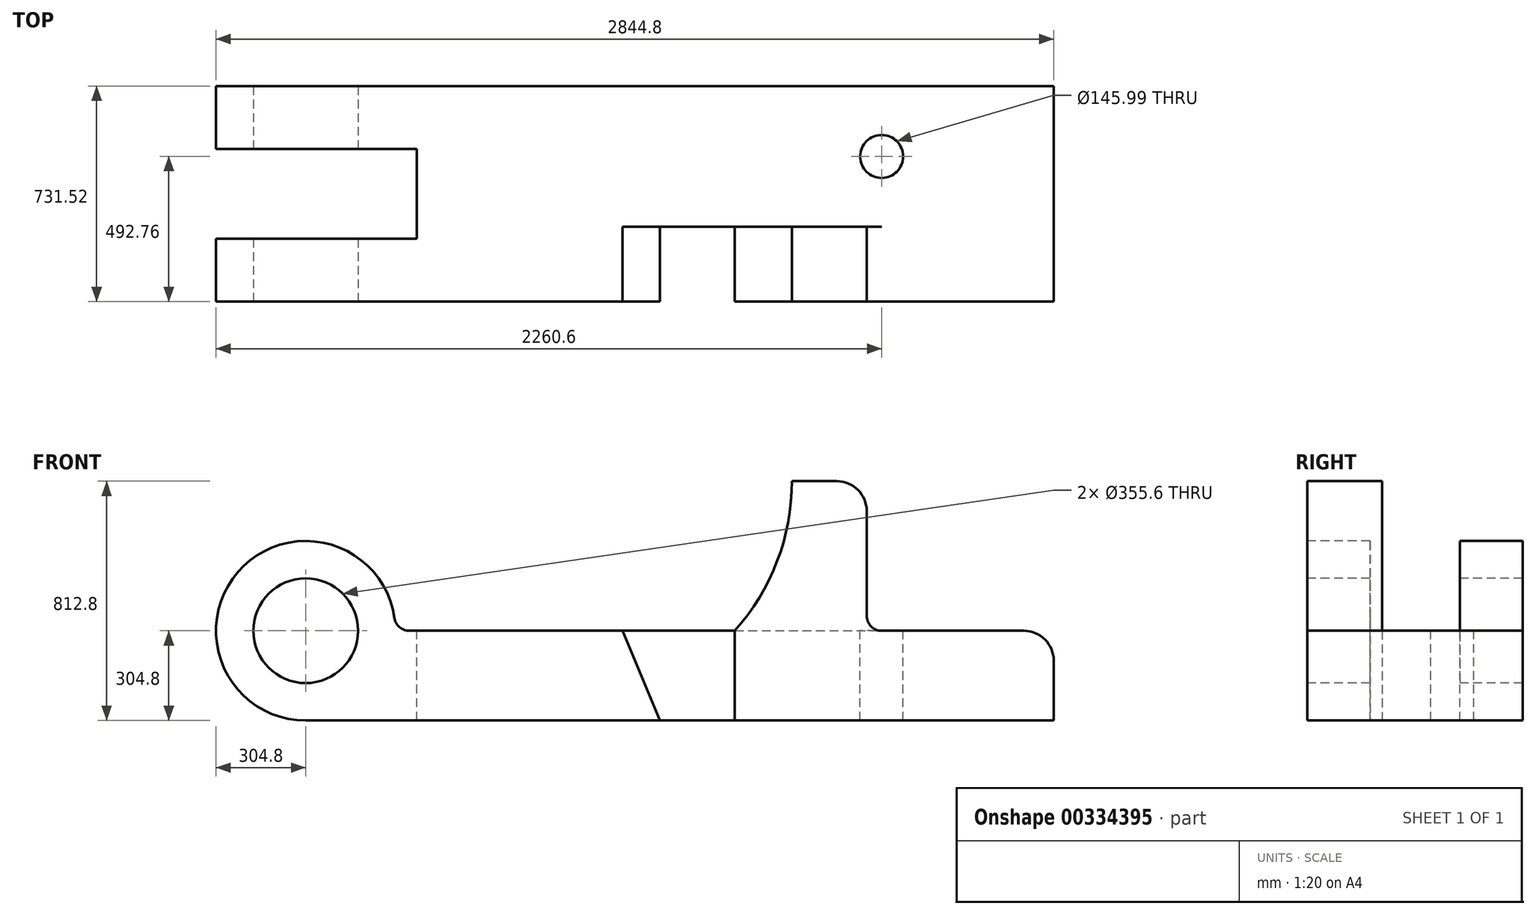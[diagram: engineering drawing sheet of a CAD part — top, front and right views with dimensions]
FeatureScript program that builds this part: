
annotation { "Feature Type Name" : "Feature", "Feature Type Description" : "" }
export const myFeature = defineFeature(function(context is Context, id is Id, definition is map)
    precondition{}
    {
        {
            var Q0;
            Q0=qCreatedBy(makeId("Front.planeOp"),FACE);
            var sketch = newSketch(context, id + "F0", { "sketchPlane" : qUnion([Q0])});
            skCircle(sketch, "E0", {"center": v(0, 0) * mm, "radius": 177.8 * mm});
            skLineSegment(sketch, "E1.top", {"start": v(0, -304.8) * mm, "end": v(1456.94, -304.8) * mm});
            skLineSegment(sketch, "E1.left", {"start": v(0, 0) * mm, "end": v(0, -304.8) * mm});
            skLineSegment(sketch, "E2", {"start": v(1651, 508) * mm, "end": v(1803.4, 508) * mm});
            skLineSegment(sketch, "E3", {"start": v(1905, 406.4) * mm, "end": v(1905, 50.8) * mm});
            skLineSegment(sketch, "E4", {"start": v(1955.8, 0) * mm, "end": v(2438.4, 0) * mm});
            skLineSegment(sketch, "E5", {"start": v(2540, -101.6) * mm, "end": v(2540, -304.8) * mm});
            skLineSegment(sketch, "E6", {"start": v(2540, -304.8) * mm, "end": v(1456.94, -304.8) * mm});
            skLineSegment(sketch, "E7", {"start": v(0, 0) * mm, "end": v(0, 1250.25) * mm});
            skLineSegment(sketch, "E8", {"start": v(351.95, 0) * mm, "end": v(1456.94, 0) * mm});
            skLineSegment(sketch, "E9", {"start": v(1075.94, 0) * mm, "end": v(1202.94, -304.8) * mm});
            skArc(sketch, "E10", {"start": v(1456.94, 0) * mm, "mid": v(1600.83, 236.1) * mm, "end": v(1651, 508) * mm});
            skLineSegment(sketch, "E11", {"start": v(1456.94, 0) * mm, "end": v(1456.94, -304.8) * mm});
            skLineSegment(sketch, "E12", {"start": v(1456.94, -304.8) * mm, "end": v(1456.94, -304.8) * mm});
            skArc(sketch, "E13", {"start": v(301.67, 43.54) * mm, "mid": v(-230.4, 199.54) * mm, "end": v(0, -304.8) * mm});
            skPoint(sketch, "E14.visualSharp", {"position": v(1905, 508) * mm});
            skArc(sketch, "E14.filletArc", {"start": v(1905, 406.4) * mm, "mid": v(1875.24, 478.24) * mm, "end": v(1803.4, 508) * mm});
            skPoint(sketch, "E15.visualSharp", {"position": v(1905, 0) * mm});
            skArc(sketch, "E15.filletArc", {"start": v(1905, 50.8) * mm, "mid": v(1919.88, 14.88) * mm, "end": v(1955.8, 0) * mm});
            skPoint(sketch, "E16.visualSharp", {"position": v(2540, 0) * mm});
            skArc(sketch, "E16.filletArc", {"start": v(2540, -101.6) * mm, "mid": v(2510.24, -29.76) * mm, "end": v(2438.4, 0) * mm});
            skLineSegment(sketch, "E17", {"start": v(1456.94, 0) * mm, "end": v(1955.8, 0) * mm});
            skPoint(sketch, "E18.visualSharp", {"position": v(304.8, 0) * mm});
            skArc(sketch, "E18.filletArc", {"start": v(301.67, 43.54) * mm, "mid": v(318.7, 12.4) * mm, "end": v(351.95, 0) * mm});
            skSolve(sketch);
        }
        {
            var Q0;
            {var subQ0=sQuery(id+"F0.wireOp",EDGE,"E1.left");var subQ1=sQuery(id+"F0.wireOp",EDGE,"E0");var subQ2=makeQuery(id+"F0.imprint","INTERSECT",VERTEX,{"derivedFrom":[subQ1,subQ0]});Q0=makeQuery(id+"F0.imprint","IMPRINT",FACE,{"disambiguationData":[TD([[makeQuery(id+"F0.imprint","IMPRINT",EDGE,{"disambiguationData":[TD([[subQ2,1.0]])],"derivedFrom":subQ1}),-1.0]])]});}
            var Q1;
            {var subQ2=sQuery(id+"F0.wireOp",EDGE,"E9");Q1=makeQuery(id+"F0.imprint","IMPRINT",FACE,{"disambiguationData":[TD([[makeQuery(id+"F0.imprint","IMPRINT",EDGE,{"derivedFrom":subQ2}),1.0]])]});}
            var Q2;
            Q2=makeQuery(id+"F0.imprint","IMPRINT",FACE,{"disambiguationData":[TD([[makeQuery(id+"F0.imprint","IMPRINT",EDGE,{"derivedFrom":sQuery(id+"F0.wireOp",EDGE,"E4")}),-1.0]])]});
            var Q3;
            {var subQ9=sQuery(id+"F0.wireOp",EDGE,"E9");Q3=makeQuery(id+"F0.imprint","IMPRINT",FACE,{"disambiguationData":[TD([[makeQuery(id+"F0.imprint","IMPRINT",EDGE,{"derivedFrom":subQ9}),-1.0]])]});}
            extrude(context, id + "F1", {"entities" : qUnion([Q0, Q1, Q2, Q3]), "oppositeDirection" : true, "depth" : 731.52 * mm});
        }
        {
            var Q0;
            {var subQ2=sQuery(id+"F0.wireOp",EDGE,"E9");Q0=makeQuery(id+"F0.imprint","IMPRINT",FACE,{"disambiguationData":[TD([[makeQuery(id+"F0.imprint","IMPRINT",EDGE,{"derivedFrom":subQ2}),1.0]])]});}
            extrude(context, id + "F2", {"entities" : qUnion([Q0]), "operationType" : NewBodyOperationType.REMOVE, "oppositeDirection" : true, "depth" : 254 * mm});
        }
        {
            var Q0;
            Q0=makeQuery(id+"F0.imprint","IMPRINT",FACE,{"disambiguationData":[TD([[makeQuery(id+"F0.imprint","IMPRINT",EDGE,{"derivedFrom":sQuery(id+"F0.wireOp",EDGE,"E2")}),-1.0]])]});
            extrude(context, id + "F3", {"entities" : qUnion([Q0]), "operationType" : NewBodyOperationType.ADD, "oppositeDirection" : true, "depth" : 254 * mm});
        }
        {
            var Q0;
            Q0=makeQuery(id+"F1.opExtrude","SWEPT_FACE",FACE,{"disambiguationData":[OSD([sQuery(id+"F0.wireOp",EDGE,"E4"),sQuery(id+"F0.wireOp",EDGE,"E8"),sQuery(id+"F0.wireOp",EDGE,"E17")])]});
            var sketch = newSketch(context, id + "F4", { "sketchPlane" : qUnion([Q0])});
            skLineSegment(sketch, "E19", {"start": v(351.95, 518.16) * mm, "end": v(-550.89, 518.16) * mm});
            skLineSegment(sketch, "E20", {"start": v(-550.89, 518.16) * mm, "end": v(-550.89, 213.36) * mm});
            skLineSegment(sketch, "E21", {"start": v(-550.89, 213.36) * mm, "end": v(351.95, 213.36) * mm});
            skLineSegment(sketch, "E22", {"start": v(351.95, 213.36) * mm, "end": v(351.95, 518.16) * mm});
            skLineSegment(sketch, "E23", {"start": v(-550.89, 213.36) * mm, "end": v(-550.89, 0) * mm});
            skLineSegment(sketch, "E24", {"start": v(-550.89, 0) * mm, "end": v(351.95, 0) * mm});
            skLineSegment(sketch, "E25", {"start": v(351.95, 0) * mm, "end": v(351.95, 213.36) * mm});
            skLineSegment(sketch, "E26", {"start": v(351.95, 518.16) * mm, "end": v(351.95, 731.52) * mm});
            skLineSegment(sketch, "E27", {"start": v(351.95, 731.52) * mm, "end": v(-550.89, 731.52) * mm});
            skLineSegment(sketch, "E28", {"start": v(-550.89, 731.52) * mm, "end": v(-550.89, 518.16) * mm});
            skCircle(sketch, "E29", {"center": v(1955.8, 492.76) * mm, "radius": 73 * mm});
            skSolve(sketch);
        }
        {
            var Q0;
            Q0=makeQuery(id+"F4.imprint","IMPRINT",FACE,{"disambiguationData":[TD([[makeQuery(id+"F4.imprint","IMPRINT",EDGE,{"derivedFrom":sQuery(id+"F4.wireOp",EDGE,"E19")}),1.0]])]});
            extrude(context, id + "F5", {"entities" : qUnion([Q0]), "operationType" : NewBodyOperationType.REMOVE, "endBound" : BoundingType.SYMMETRIC, "oppositeDirection" : true, "depth" : 919.48 * mm});
        }
        {
            var Q0;
            Q0=makeQuery(id+"F4.imprint","IMPRINT",FACE,{"disambiguationData":[TD([[makeQuery(id+"F4.imprint","IMPRINT",EDGE,{"derivedFrom":sQuery(id+"F4.wireOp",EDGE,"E29")}),1.0]])]});
            var Q1;
            Q1=sQuery(id+"F4.wireOp",EDGE,"E29");
            extrude(context, id + "F6", {"entities" : qUnion([Q0]), "operationType" : NewBodyOperationType.REMOVE, "surfaceEntities" : qUnion([Q1]), "oppositeDirection" : true, "depth" : 408.94 * mm});
        }
        {
            var Q0;
            Q0=makeQuery(id+"F5.boolean.opBoolean","COPY",FACE,{"derivedFrom":makeQuery(id+"F5.opExtrude","SWEPT_FACE",FACE,{"disambiguationData":[OSD([sQuery(id+"F4.wireOp",EDGE,"E22")])]})});
            extrude(context, id + "F7", {"entities" : qUnion([Q0]), "operationType" : NewBodyOperationType.REMOVE, "oppositeDirection" : true, "depth" : 25.4 * mm});
        }
    });
